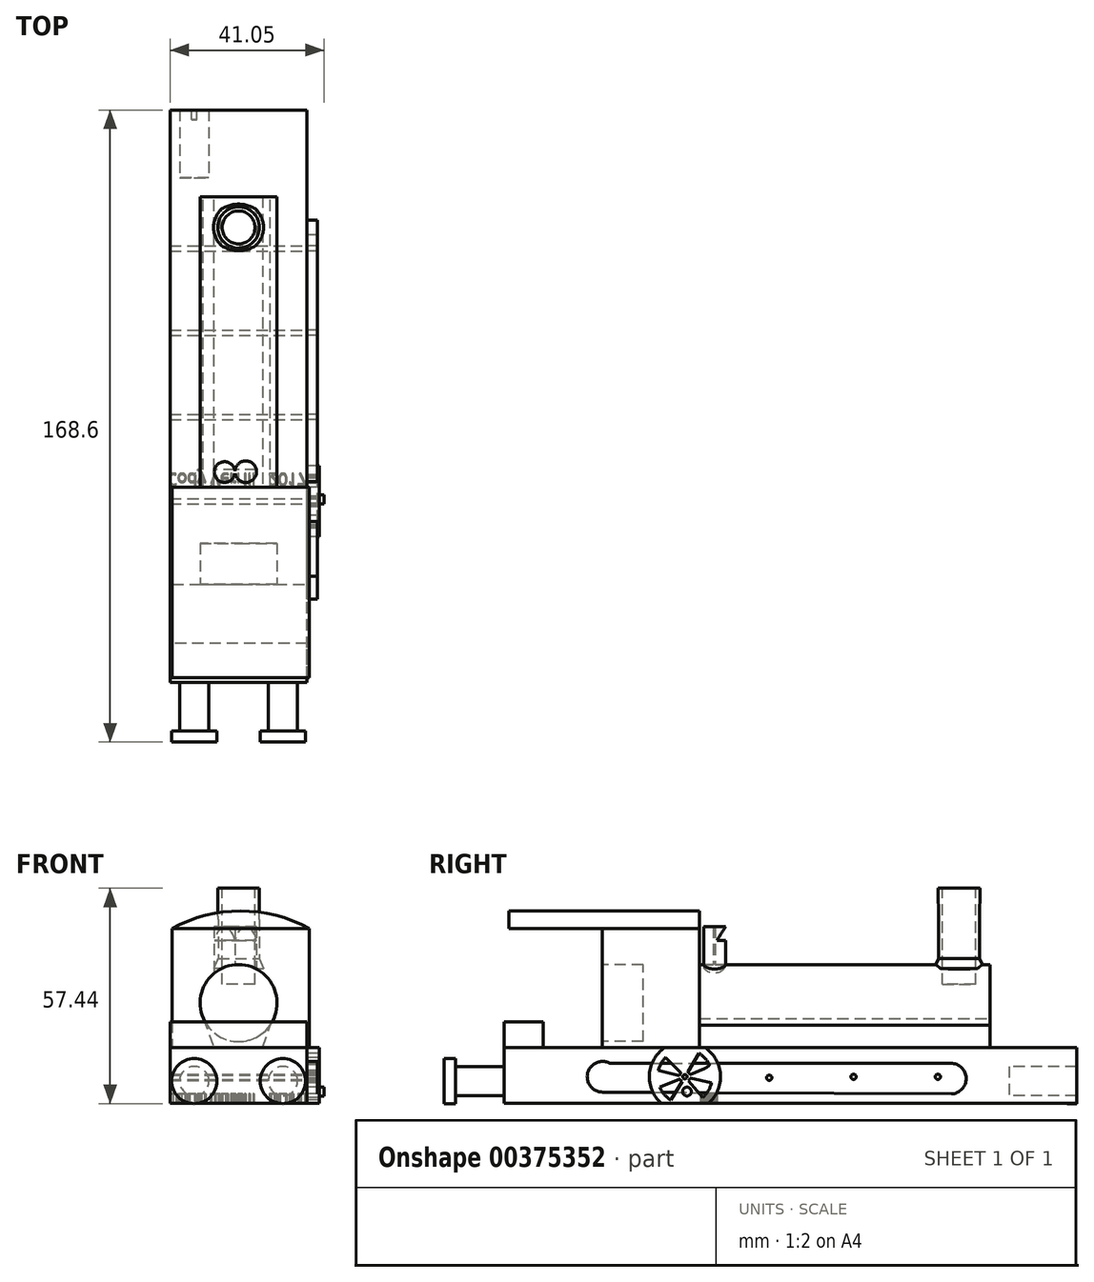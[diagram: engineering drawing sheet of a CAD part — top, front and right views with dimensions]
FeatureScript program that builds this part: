
annotation { "Feature Type Name" : "Feature", "Feature Type Description" : "" }
export const myFeature = defineFeature(function(context is Context, id is Id, definition is map)
    precondition{}
    {
        {
            var Q0;
            Q0=qCreatedBy(makeId("Front.planeOp"),FACE);
            var sketch = newSketch(context, id + "F0", { "sketchPlane" : qUnion([Q0])});
            skCircle(sketch, "E0", {"center": v(0, 91.63) * mm, "radius": 10.27 * mm});
            skSolve(sketch);
        }
        {
            var Q0;
            Q0=makeQuery(id+"F0.imprint","IMPRINT",FACE,{"disambiguationData":[TD([[makeQuery(id+"F0.imprint","IMPRINT",EDGE,{"derivedFrom":sQuery(id+"F0.wireOp",EDGE,"E0")}),1.0]])]});
            extrude(context, id + "F1", {"entities" : qUnion([Q0]), "depth" : 77.47 * mm});
        }
        {
            var Q0;
            Q0=makeQuery(id+"F1.opExtrude","CAP_FACE",FACE,{"disambiguationData":[OSD([sQuery(id+"F0.wireOp",EDGE,"E0")])],"isStart":false});
            var sketch = newSketch(context, id + "F2", { "sketchPlane" : qUnion([Q0])});
            skLineSegment(sketch, "E1.bottom", {"start": v(-17.68, 111.5) * mm, "end": v(18.8, 111.5) * mm});
            skLineSegment(sketch, "E1.top", {"start": v(-17.68, 79.8) * mm, "end": v(18.8, 79.8) * mm});
            skLineSegment(sketch, "E1.left", {"start": v(-17.68, 111.5) * mm, "end": v(-17.68, 79.8) * mm});
            skLineSegment(sketch, "E1.right", {"start": v(18.8, 111.5) * mm, "end": v(18.8, 79.8) * mm});
            skArc(sketch, "E2", {"start": v(18.8, 111.5) * mm, "mid": v(0.56, 116.2) * mm, "end": v(-17.68, 111.5) * mm});
            skSolve(sketch);
        }
        {
            var Q0;
            Q0=makeQuery(id+"F2.imprint","IMPRINT",FACE,{"disambiguationData":[TD([[makeQuery(id+"F2.imprint","IMPRINT",EDGE,{"derivedFrom":sQuery(id+"F2.wireOp",EDGE,"E1.bottom")}),1.0]])]});
            var Q1;
            Q1=makeQuery(id+"F2.imprint","IMPRINT",FACE,{"disambiguationData":[TD([[makeQuery(id+"F2.imprint","IMPRINT",EDGE,{"derivedFrom":sQuery(id+"F2.wireOp",EDGE,"E1.bottom")}),-1.0]])]});
            var Q2;
            Q2=makeQuery(id+"F2.imprint","IMPRINT",FACE,{"disambiguationData":[TD([[makeQuery(id+"F2.imprint","IMPRINT",EDGE,{"derivedFrom":makeQuery(id+"F1.opExtrude","CAP_EDGE",EDGE,{"disambiguationData":[OSD([sQuery(id+"F0.wireOp",EDGE,"E0")])],"isStart":false})}),1.0]])]});
            extrude(context, id + "F3", {"entities" : qUnion([Q0, Q1, Q2]), "depth" : 25.9 * mm});
        }
        {
            var Q0;
            Q0=makeQuery(id+"F3.opExtrude","CAP_FACE",FACE,{"disambiguationData":[OSD([sQuery(id+"F0.wireOp",EDGE,"E0"),sQuery(id+"F2.wireOp",EDGE,"E1.top"),sQuery(id+"F2.wireOp",EDGE,"E1.left"),sQuery(id+"F2.wireOp",EDGE,"E1.right"),sQuery(id+"F2.wireOp",EDGE,"E2")])],"isStart":false});
            var sketch = newSketch(context, id + "F4", { "sketchPlane" : qUnion([Q0])});
            skLineSegment(sketch, "E3", {"start": v(-17.68, 111.5) * mm, "end": v(18.8, 111.5) * mm});
            skSolve(sketch);
        }
        {
            var Q0;
            Q0=makeQuery(id+"F4.imprint","IMPRINT",FACE,{"disambiguationData":[TD([[makeQuery(id+"F4.imprint","IMPRINT",EDGE,{"derivedFrom":sQuery(id+"F4.wireOp",EDGE,"E3")}),1.0]])]});
            extrude(context, id + "F5", {"entities" : qUnion([Q0]), "operationType" : NewBodyOperationType.ADD, "depth" : 24.9 * mm});
        }
        {
            var Q0;
            Q0=qCreatedBy(makeId("Front.planeOp"),FACE);
            var sketch = newSketch(context, id + "F6", { "sketchPlane" : qUnion([Q0])});
            skLineSegment(sketch, "E4.top", {"start": v(14.24, 65.38) * mm, "end": v(-13.5, 65.38) * mm});
            skLineSegment(sketch, "E4.left", {"start": v(14.24, 78.57) * mm, "end": v(14.24, 65.38) * mm});
            skLineSegment(sketch, "E4.right", {"start": v(-13.5, 78.57) * mm, "end": v(-13.5, 65.38) * mm});
            skLineSegment(sketch, "E5", {"start": v(14.24, 78.57) * mm, "end": v(-13.5, 78.57) * mm});
            skLineSegment(sketch, "E6", {"start": v(-9.81, 88.6) * mm, "end": v(-6.1, 78.57) * mm});
            skCircle(sketch, "E7.0", {"center": v(0, 91.63) * mm, "radius": 10.27 * mm});
            skLineSegment(sketch, "E8", {"start": v(6.01, 78.57) * mm, "end": v(8.4, 85.72) * mm});
            skSolve(sketch);
        }
        {
            var Q0;
            Q0=makeQuery(id+"F6.imprint","IMPRINT",FACE,{"disambiguationData":[TD([[makeQuery(id+"F6.imprint","IMPRINT",EDGE,{"derivedFrom":sQuery(id+"F6.wireOp",EDGE,"E4.top")}),-1.0]])]});
            var Q1;
            {var subQ3=sQuery(id+"F6.wireOp",EDGE,"E8");Q1=makeQuery(id+"F6.imprint","IMPRINT",FACE,{"disambiguationData":[TD([[makeQuery(id+"F6.imprint","IMPRINT",EDGE,{"derivedFrom":subQ3}),1.0]])]});}
            extrude(context, id + "F7", {"entities" : qUnion([Q0, Q1]), "operationType" : NewBodyOperationType.ADD, "depth" : 78.74 * mm});
        }
        {
            var Q0;
            Q0=qCreatedBy(makeId("Front.planeOp"),FACE);
            var sketch = newSketch(context, id + "F8", { "sketchPlane" : qUnion([Q0])});
            skLineSegment(sketch, "E9.bottom", {"start": v(18.25, 79.8) * mm, "end": v(-18.25, 79.8) * mm});
            skLineSegment(sketch, "E9.left", {"start": v(18.25, 79.8) * mm, "end": v(18.25, 64.86) * mm});
            skLineSegment(sketch, "E9.right", {"start": v(-18.25, 79.8) * mm, "end": v(-18.25, 64.86) * mm});
            skLineSegment(sketch, "E10", {"start": v(-18.25, 64.86) * mm, "end": v(18.25, 64.86) * mm});
            skSolve(sketch);
        }
        {
            var Q0;
            Q0 = qSketchRegion(id + "F8", true);
            extrude(context, id + "F9", {"entities" : qUnion([Q0]), "operationType" : NewBodyOperationType.ADD, "depth" : 129.54 * mm, "hasSecondDirection" : true, "secondDirectionOppositeDirection" : true, "secondDirectionDepth" : 5.08 * mm});
        }
        {
            var Q0;
            Q0=qCreatedBy(makeId("Top.planeOp"),FACE);
            cPlane(context, id + "F10", {"entities" : qUnion([Q0]), "cplaneType" : CPlaneType.OFFSET, "offset" : 95.25 * mm, "width" : 152.4 * mm, "height" : 152.4 * mm});
        }
        {
            var Q0;
            Q0=qCreatedBy(id+"F10.planeOp",FACE);
            var sketch = newSketch(context, id + "F11", { "sketchPlane" : qUnion([Q0])});
            skCircle(sketch, "E11", {"center": v(1.92, -73.37) * mm, "radius": 2.88 * mm});
            skCircle(sketch, "E12", {"center": v(-3.73, -73.47) * mm, "radius": 2.77 * mm});
            skLineSegment(sketch, "E13.bottom", {"start": v(-0.4, -73.79) * mm, "end": v(-2.1, -73.79) * mm});
            skLineSegment(sketch, "E13.top", {"start": v(-0.4, -73.24) * mm, "end": v(-2.1, -73.24) * mm});
            skLineSegment(sketch, "E13.left", {"start": v(-0.4, -73.79) * mm, "end": v(-0.4, -73.24) * mm});
            skLineSegment(sketch, "E13.right", {"start": v(-2.1, -73.79) * mm, "end": v(-2.1, -73.24) * mm});
            skPoint(sketch, "E13.middle", {"position": v(-1.25, -73.52) * mm});
            skSolve(sketch);
        }
        {
            var Q0;
            Q0 = qSketchRegion(id + "F11", true);
            extrude(context, id + "F12", {"entities" : qUnion([Q0]), "operationType" : NewBodyOperationType.ADD, "depth" : 16.76 * mm});
        }
        {
            var Q0;
            Q0=qCreatedBy(makeId("Right.planeOp"),FACE);
            var sketch = newSketch(context, id + "F13", { "sketchPlane" : qUnion([Q0])});
            skLineSegment(sketch, "E14", {"start": v(-70.17, 108.34) * mm, "end": v(-72.79, 108.34) * mm});
            skLineSegment(sketch, "E15", {"start": v(-72.79, 108.34) * mm, "end": v(-70.1, 112.6) * mm});
            skLineSegment(sketch, "E16", {"start": v(-70.1, 112.6) * mm, "end": v(-70.17, 108.34) * mm});
            skSolve(sketch);
        }
        {
            var Q0;
            Q0=makeQuery(id+"F13.imprint","IMPRINT",FACE,{"disambiguationData":[TD([[makeQuery(id+"F13.imprint","IMPRINT",EDGE,{"derivedFrom":sQuery(id+"F13.wireOp",EDGE,"E14")}),-1.0]])]});
            extrude(context, id + "F14", {"entities" : qUnion([Q0]), "operationType" : NewBodyOperationType.REMOVE, "endBound" : BoundingType.THROUGH_ALL, "depth" : 25.4 * mm, "hasSecondDirection" : true, "secondDirectionBound" : SecondDirectionBoundingType.THROUGH_ALL, "secondDirectionOppositeDirection" : true, "secondDirectionDepth" : 25.4 * mm});
        }
        {
            var Q0;
            Q0=makeQuery(id+"F13.imprint","IMPRINT",FACE,{"disambiguationData":[TD([[makeQuery(id+"F13.imprint","IMPRINT",EDGE,{"derivedFrom":sQuery(id+"F13.wireOp",EDGE,"E14")}),-1.0]])]});
            extrude(context, id + "F15", {"entities" : qUnion([Q0]), "operationType" : NewBodyOperationType.REMOVE, "depth" : 25.4 * mm});
        }
        {
            var Q0;
            Q0=qCreatedBy(makeId("Right.planeOp"),FACE);
            var sketch = newSketch(context, id + "F16", { "sketchPlane" : qUnion([Q0])});
            skLineSegment(sketch, "E17", {"start": v(-2.75, 113.9) * mm, "end": v(-2.75, 103.55) * mm});
            skLineSegment(sketch, "E18", {"start": v(-2.75, 103.55) * mm, "end": v(-1.55, 100.87) * mm});
            skLineSegment(sketch, "E19", {"start": v(-8.2, 100.22) * mm, "end": v(-1.55, 100.87) * mm});
            skLineSegment(sketch, "E20", {"start": v(-8.2, 100.22) * mm, "end": v(-8.2, 122.25) * mm});
            skLineSegment(sketch, "E21", {"start": v(-8.2, 122.25) * mm, "end": v(-2.67, 122.25) * mm});
            skLineSegment(sketch, "E22", {"start": v(-2.75, 113.9) * mm, "end": v(-2.67, 122.25) * mm});
            skSolve(sketch);
        }
        {
            var Q0;
            Q0=makeQuery(id+"F16.imprint","IMPRINT",FACE,{"disambiguationData":[TD([[makeQuery(id+"F16.imprint","IMPRINT",EDGE,{"derivedFrom":sQuery(id+"F16.wireOp",EDGE,"E17")}),-1.0]])]});
            var Q1;
            Q1=sQuery(id+"F16.wireOp",EDGE,"E20");
            revolve(context, id + "F17", {"operationType" : NewBodyOperationType.ADD, "entities" : qUnion([Q0]), "axis" : qUnion([Q1]), "revolveType" : RevolveType.FULL});
        }
        {
            var Q0;
            Q0=makeQuery(id+"F9.opExtrude","SWEPT_FACE",FACE,{"disambiguationData":[OSD([sQuery(id+"F8.wireOp",EDGE,"E9.left")])]});
            var sketch = newSketch(context, id + "F18", { "sketchPlane" : qUnion([Q0])});
            skPoint(sketch, "E23.center", {"position": v(0, 0) * mm});
            skLineSegment(sketch, "E24", {"start": v(-79.94, 72.54) * mm, "end": v(-76, 74.2) * mm});
            skArc(sketch, "E25", {"start": v(-88, 69.15) * mm, "mid": v(-86.8, 67.22) * mm, "end": v(-85.06, 65.75) * mm});
            skLineSegment(sketch, "E26.1.0", {"start": v(-80.54, 73.23) * mm, "end": v(-77.53, 78.2) * mm});
            skLineSegment(sketch, "E26.4.0", {"start": v(-82.73, 72.3) * mm, "end": v(-88.38, 73.63) * mm});
            skLineSegment(sketch, "E26.5.0", {"start": v(-82.65, 71.4) * mm, "end": v(-88, 69.15) * mm});
            skLineSegment(sketch, "E26.6.0", {"start": v(-82.06, 70.71) * mm, "end": v(-85.06, 65.75) * mm});
            skLineSegment(sketch, "E26.8.0", {"start": v(-80.34, 70.86) * mm, "end": v(-76.54, 66.47) * mm});
            skLineSegment(sketch, "E26.9.0", {"start": v(-79.87, 71.63) * mm, "end": v(-74.22, 70.31) * mm});
            skPoint(sketch, "E27.center.orphan", {"position": v(-44.54, 71.07) * mm});
            skCircle(sketch, "E28.MirrorC", {"center": v(-61.62, 71.97) * mm, "radius": 7.27 * mm});
            skLineSegment(sketch, "E29.MirrorCS", {"start": v(-61.62, 71.97) * mm, "end": v(-55.37, 73.17) * mm});
            skLineSegment(sketch, "E30.MirrorCS", {"start": v(-61.62, 71.97) * mm, "end": v(-57.27, 76.61) * mm});
            skLineSegment(sketch, "E31.MirrorCS", {"start": v(-61.62, 71.97) * mm, "end": v(-60.83, 78.28) * mm});
            skLineSegment(sketch, "E32.MirrorCS", {"start": v(-61.62, 71.97) * mm, "end": v(-64.7, 77.54) * mm});
            skLineSegment(sketch, "E33.MirrorCS", {"start": v(-61.62, 71.97) * mm, "end": v(-67.38, 74.67) * mm});
            skLineSegment(sketch, "E34.MirrorCS", {"start": v(-61.62, 71.97) * mm, "end": v(-67.87, 70.77) * mm});
            skLineSegment(sketch, "E35.MirrorCS", {"start": v(-61.62, 71.97) * mm, "end": v(-65.97, 67.33) * mm});
            skLineSegment(sketch, "E36.MirrorCS", {"start": v(-61.62, 71.97) * mm, "end": v(-62.41, 65.66) * mm});
            skLineSegment(sketch, "E37.MirrorCS", {"start": v(-61.62, 71.97) * mm, "end": v(-58.55, 66.4) * mm});
            skLineSegment(sketch, "E38.MirrorCS", {"start": v(-61.62, 71.97) * mm, "end": v(-55.86, 69.27) * mm});
            skCircle(sketch, "E39.MirrorC", {"center": v(-61.73, 71.74) * mm, "radius": 6.37 * mm});
            skLineSegment(sketch, "E40.MirrorCS", {"start": v(-43.2, 71.97) * mm, "end": v(-47.55, 76.61) * mm});
            skLineSegment(sketch, "E41.MirrorCS", {"start": v(-43.2, 71.97) * mm, "end": v(-43.99, 78.28) * mm});
            skLineSegment(sketch, "E42.MirrorCS", {"start": v(-43.2, 71.97) * mm, "end": v(-40.13, 77.54) * mm});
            skLineSegment(sketch, "E43.MirrorCS", {"start": v(-43.2, 71.97) * mm, "end": v(-37.44, 74.67) * mm});
            skLineSegment(sketch, "E44.MirrorCS", {"start": v(-43.2, 71.97) * mm, "end": v(-36.95, 70.77) * mm});
            skLineSegment(sketch, "E45.MirrorCS", {"start": v(-43.2, 71.97) * mm, "end": v(-38.85, 67.33) * mm});
            skLineSegment(sketch, "E46.MirrorCS", {"start": v(-43.2, 71.97) * mm, "end": v(-42.4, 65.66) * mm});
            skLineSegment(sketch, "E47.MirrorCS", {"start": v(-43.2, 71.97) * mm, "end": v(-48.96, 69.27) * mm});
            skLineSegment(sketch, "E48.MirrorCS", {"start": v(-43.2, 71.97) * mm, "end": v(-49.45, 73.17) * mm});
            skCircle(sketch, "E49.MirrorC", {"center": v(-43.1, 71.74) * mm, "radius": 6.37 * mm});
            skCircle(sketch, "E50.MirrorC", {"center": v(-43.2, 71.97) * mm, "radius": 7.27 * mm});
            skLineSegment(sketch, "E51", {"start": v(-43.1, 71.74) * mm, "end": v(-47.38, 67.03) * mm});
            skArc(sketch, "E52", {"start": v(-82.65, 71.4) * mm, "mid": v(-82.41, 71) * mm, "end": v(-82.06, 70.71) * mm});
            skArc(sketch, "E53.trimOffspring", {"start": v(-82.35, 73) * mm, "mid": v(-82.59, 72.68) * mm, "end": v(-82.73, 72.3) * mm});
            skArc(sketch, "E54.trimOffspring", {"start": v(-79.94, 72.54) * mm, "mid": v(-80.19, 72.93) * mm, "end": v(-80.54, 73.23) * mm});
            skArc(sketch, "E55.trimOffspring", {"start": v(-80.34, 70.86) * mm, "mid": v(-80.04, 71.2) * mm, "end": v(-79.87, 71.63) * mm});
            skCircle(sketch, "E56", {"center": v(-81.3, 71.97) * mm, "radius": 0.57 * mm});
            skArc(sketch, "E57.filletArc", {"start": v(-76, 74.2) * mm, "mid": v(-75.32, 74.6) * mm, "end": v(-74.75, 75.13) * mm});
            skLineSegment(sketch, "E58", {"start": v(-86.49, 77.07) * mm, "end": v(-82.35, 73) * mm});
            skArc(sketch, "E59.trimOffspring", {"start": v(-86.49, 77.07) * mm, "mid": v(-87.67, 75.48) * mm, "end": v(-88.38, 73.63) * mm});
            skArc(sketch, "E60.trimOffspring", {"start": v(-76.54, 66.47) * mm, "mid": v(-75.08, 68.2) * mm, "end": v(-74.22, 70.31) * mm});
            skArc(sketch, "E61.trimOffspring", {"start": v(-74.75, 75.13) * mm, "mid": v(-75.92, 76.86) * mm, "end": v(-77.53, 78.2) * mm});
            skCircle(sketch, "E62", {"center": v(-81.3, 71.97) * mm, "radius": 9.47 * mm});
            skCircle(sketch, "E63", {"center": v(-81.3, 71.97) * mm, "radius": 7.27 * mm, "construction": true});
            skSolve(sketch);
        }
        {
            var Q0;
            Q0=makeQuery(id+"F18.imprint","IMPRINT",FACE,{"disambiguationData":[TD([[makeQuery(id+"F18.imprint","IMPRINT",EDGE,{"derivedFrom":sQuery(id+"F18.wireOp",EDGE,"E24")}),-1.0]])]});
            var Q1;
            {var subQ0=sQuery(id+"F18.wireOp",EDGE,"E62");var subQ1=makeQuery(id+"F9.opExtrude","SWEPT_EDGE",EDGE,{"disambiguationData":[OSD([sQuery(id+"F8.wireOp",EDGE,"E9.left"),sQuery(id+"F8.wireOp",EDGE,"E10")])]});var subQ2=makeQuery(id+"F18.imprint","INTERSECT",VERTEX,{"disambiguationData":[OD(0.0)],"derivedFrom":[subQ1,subQ0]});Q1=makeQuery(id+"F18.imprint","IMPRINT",FACE,{"disambiguationData":[TD([[makeQuery(id+"F18.imprint","IMPRINT",EDGE,{"disambiguationData":[TD([[subQ2,-1.0]])],"derivedFrom":subQ0}),1.0]])]});}
            var Q2;
            {var subQ0=sQuery(id+"F18.wireOp",EDGE,"E62");var subQ1=makeQuery(id+"F9.opExtrude","SWEPT_EDGE",EDGE,{"disambiguationData":[OSD([sQuery(id+"F8.wireOp",EDGE,"E9.bottom"),sQuery(id+"F8.wireOp",EDGE,"E9.left")])]});var subQ2=makeQuery(id+"F18.imprint","INTERSECT",VERTEX,{"disambiguationData":[OD(0.0)],"derivedFrom":[subQ1,subQ0]});Q2=makeQuery(id+"F18.imprint","IMPRINT",FACE,{"disambiguationData":[TD([[makeQuery(id+"F18.imprint","IMPRINT",EDGE,{"disambiguationData":[TD([[subQ2,1.0]])],"derivedFrom":subQ0}),1.0]])]});}
            extrude(context, id + "F19", {"entities" : qUnion([Q0, Q1, Q2]), "depth" : 3.3 * mm});
        }
        {
            var Q0;
            {var subQ0=sQuery(id+"F8.wireOp",EDGE,"E9.left");var subQ11=makeQuery(id+"F9.opExtrude","CAP_EDGE",EDGE,{"disambiguationData":[OSD([subQ0])],"isStart":true});Q0=makeQuery(id+"F18.imprint","IMPRINT",FACE,{"disambiguationData":[TD([[makeQuery(id+"F18.imprint","IMPRINT",EDGE,{"derivedFrom":subQ11}),-1.0]])]});}
            var sketch = newSketch(context, id + "F20", { "sketchPlane" : qUnion([Q0])});
            skCircle(sketch, "E64", {"center": v(-81.3, 71.97) * mm, "radius": 0.7 * mm});
            skCircle(sketch, "E65.MirrorC", {"center": v(-36.34, 71.96) * mm, "radius": 0.7 * mm});
            skArc(sketch, "E66", {"start": v(-101.27, 75.56) * mm, "mid": v(-107.2, 72.99) * mm, "end": v(-103.26, 67.86) * mm});
            skPoint(sketch, "E67.MirrorC.center.orphan", {"position": v(-58.82, 71.71) * mm});
            skCircle(sketch, "E68", {"center": v(-58.82, 71.71) * mm, "radius": 0.7 * mm});
            skCircle(sketch, "E69", {"center": v(-13.86, 71.96) * mm, "radius": 0.7 * mm});
            skLineSegment(sketch, "E70", {"start": v(-101.27, 75.56) * mm, "end": v(-10.43, 75.56) * mm});
            skLineSegment(sketch, "E71", {"start": v(-103.26, 67.86) * mm, "end": v(-10.25, 67.37) * mm});
            skArc(sketch, "E72", {"start": v(-10.25, 67.37) * mm, "mid": v(-6.33, 71.55) * mm, "end": v(-10.43, 75.56) * mm});
            skSolve(sketch);
        }
        {
            var Q0;
            Q0=makeQuery(id+"F20.imprint","IMPRINT",FACE,{"disambiguationData":[TD([[makeQuery(id+"F20.imprint","IMPRINT",EDGE,{"derivedFrom":sQuery(id+"F20.wireOp",EDGE,"E68")}),1.0]])]});
            var Q1;
            Q1=makeQuery(id+"F20.imprint","IMPRINT",FACE,{"disambiguationData":[TD([[makeQuery(id+"F20.imprint","IMPRINT",EDGE,{"derivedFrom":sQuery(id+"F20.wireOp",EDGE,"E64")}),1.0]])]});
            var Q2;
            {var subQ0=sQuery(id+"F20.wireOp",EDGE,"E65.MirrorC");var subQ1=sQuery(id+"F18.wireOp",EDGE,"E50.MirrorC");var subQ2=makeQuery(id+"F9.opExtrude","SWEPT_EDGE",EDGE,{"disambiguationData":[OSD([sQuery(id+"F8.wireOp",EDGE,"E9.left"),sQuery(id+"F8.wireOp",EDGE,"E10")])]});var subQ3=makeQuery(id+"F18.imprint","IMPRINT",EDGE,{"disambiguationData":[TD([[makeQuery(id+"F18.imprint","INTERSECT",VERTEX,{"disambiguationData":[OD(0.0)],"derivedFrom":[subQ2,subQ1]}),-1.0]])],"derivedFrom":subQ1});var subQ4=makeQuery(id+"F20.imprint","INTERSECT",VERTEX,{"disambiguationData":[OD(0.0)],"derivedFrom":[subQ3,subQ0]});Q2=makeQuery(id+"F20.imprint","IMPRINT",FACE,{"disambiguationData":[TD([[makeQuery(id+"F20.imprint","IMPRINT",EDGE,{"disambiguationData":[TD([[subQ4,1.0]])],"derivedFrom":subQ0}),1.0]])]});}
            var Q3;
            {var subQ0=sQuery(id+"F20.wireOp",EDGE,"E65.MirrorC");var subQ1=sQuery(id+"F18.wireOp",EDGE,"E50.MirrorC");var subQ2=makeQuery(id+"F9.opExtrude","SWEPT_EDGE",EDGE,{"disambiguationData":[OSD([sQuery(id+"F8.wireOp",EDGE,"E9.left"),sQuery(id+"F8.wireOp",EDGE,"E10")])]});var subQ3=makeQuery(id+"F18.imprint","IMPRINT",EDGE,{"disambiguationData":[TD([[makeQuery(id+"F18.imprint","INTERSECT",VERTEX,{"disambiguationData":[OD(0.0)],"derivedFrom":[subQ2,subQ1]}),-1.0]])],"derivedFrom":subQ1});var subQ4=makeQuery(id+"F20.imprint","INTERSECT",VERTEX,{"disambiguationData":[OD(0.0)],"derivedFrom":[subQ3,subQ0]});Q3=makeQuery(id+"F20.imprint","IMPRINT",FACE,{"disambiguationData":[TD([[makeQuery(id+"F20.imprint","IMPRINT",EDGE,{"disambiguationData":[TD([[subQ4,-1.0]])],"derivedFrom":subQ0}),1.0]])]});}
            var Q4;
            Q4=makeQuery(id+"F20.imprint","IMPRINT",FACE,{"disambiguationData":[TD([[makeQuery(id+"F20.imprint","IMPRINT",EDGE,{"derivedFrom":sQuery(id+"F20.wireOp",EDGE,"E69")}),1.0]])]});
            extrude(context, id + "F21", {"entities" : qUnion([Q0, Q1, Q2, Q3, Q4]), "operationType" : NewBodyOperationType.REMOVE, "endBound" : BoundingType.THROUGH_ALL, "oppositeDirection" : true, "depth" : 25.4 * mm});
        }
        {
            var Q0;
            Q0 = qSketchRegion(id + "F20", true);
            extrude(context, id + "F22", {"entities" : qUnion([Q0]), "depth" : 2.8 * mm});
        }
        {
            var Q0;
            Q0=makeQuery(id+"F19.opExtrude","CAP_FACE",FACE,{"disambiguationData":[OSD([sQuery(id+"F8.wireOp",EDGE,"E9.left"),sQuery(id+"F8.wireOp",EDGE,"E10"),sQuery(id+"F18.wireOp",EDGE,"E24"),sQuery(id+"F18.wireOp",EDGE,"E25"),sQuery(id+"F18.wireOp",EDGE,"E26.1.0"),sQuery(id+"F18.wireOp",EDGE,"E26.4.0"),sQuery(id+"F18.wireOp",EDGE,"E26.5.0"),sQuery(id+"F18.wireOp",EDGE,"E26.6.0"),sQuery(id+"F18.wireOp",EDGE,"E26.8.0"),sQuery(id+"F18.wireOp",EDGE,"E26.9.0"),sQuery(id+"F18.wireOp",EDGE,"0c8bdb6e-3c98-4d02-b736-932f722b0c7a.trimOffspring"),sQuery(id+"F18.wireOp",EDGE,"1BuqDyHR-VqEz-mvgE-IeDF-BNDoeJWoOokS"),sQuery(id+"F18.wireOp",EDGE,"640e9c71-0b7e-4dc1-b20b-68745f9d8d1d.trimOffspring"),sQuery(id+"F18.wireOp",EDGE,"18493bf5-1e1e-4aa6-ba80-e87df5e9a334.trimOffspring"),sQuery(id+"F18.wireOp",EDGE,"E56"),sQuery(id+"F18.wireOp",EDGE,"fb07b3ba-5013-41e2-a678-10b8c0feb796.trimOffspring"),sQuery(id+"F18.wireOp",EDGE,"E57.filletArc"),sQuery(id+"F18.wireOp",EDGE,"E58"),sQuery(id+"F18.wireOp",EDGE,"E53.trimOffspring"),sQuery(id+"F18.wireOp",EDGE,"E55.trimOffspring"),sQuery(id+"F18.wireOp",EDGE,"E52"),sQuery(id+"F18.wireOp",EDGE,"E54.trimOffspring")])],"isStart":false});
            var sketch = newSketch(context, id + "F23", { "sketchPlane" : qUnion([Q0])});
            skCircle(sketch, "E73", {"center": v(-80.75, 68.01) * mm, "radius": 1.17 * mm});
            skSolve(sketch);
        }
        {
            var Q0;
            Q0=makeQuery(id+"F23.imprint","IMPRINT",FACE,{"disambiguationData":[TD([[makeQuery(id+"F23.imprint","IMPRINT",EDGE,{"derivedFrom":sQuery(id+"F23.wireOp",EDGE,"E73")}),1.0]])]});
            extrude(context, id + "F24", {"entities" : qUnion([Q0]), "operationType" : NewBodyOperationType.ADD, "depth" : 1.24 * mm});
        }
        {
            var Q0;
            Q0=makeQuery(id+"F17.opRevolve","SWEPT_FACE",FACE,{"disambiguationData":[OSD([sQuery(id+"F16.wireOp",EDGE,"E21")])]});
            var sketch = newSketch(context, id + "F25", { "sketchPlane" : qUnion([Q0])});
            skCircle(sketch, "E74", {"center": v(0, -8.2) * mm, "radius": 4.38 * mm});
            skSolve(sketch);
        }
        {
            var Q0;
            Q0=makeQuery(id+"F25.imprint","IMPRINT",FACE,{"disambiguationData":[TD([[makeQuery(id+"F25.imprint","IMPRINT",EDGE,{"derivedFrom":sQuery(id+"F25.wireOp",EDGE,"E74")}),1.0]])]});
            extrude(context, id + "F26", {"entities" : qUnion([Q0]), "operationType" : NewBodyOperationType.REMOVE, "oppositeDirection" : true, "depth" : 25.65 * mm});
        }
        {
            var Q0;
            Q0=makeQuery(id+"F9.opExtrude","CAP_FACE",FACE,{"disambiguationData":[OSD([sQuery(id+"F8.wireOp",EDGE,"E9.bottom"),sQuery(id+"F8.wireOp",EDGE,"E9.left"),sQuery(id+"F8.wireOp",EDGE,"E9.right"),sQuery(id+"F8.wireOp",EDGE,"E10")])],"isStart":true});
            var sketch = newSketch(context, id + "F27", { "sketchPlane" : qUnion([Q0])});
            skCircle(sketch, "E75", {"center": v(-11.82, 70.82) * mm, "radius": 3.9 * mm});
            skLineSegment(sketch, "E76", {"start": v(0, 78.45) * mm, "end": v(0, 64.86) * mm});
            skCircle(sketch, "E77.MirrorC", {"center": v(11.82, 70.82) * mm, "radius": 3.9 * mm});
            skSolve(sketch);
        }
        {
            var Q0;
            Q0=makeQuery(id+"F27.imprint","IMPRINT",FACE,{"disambiguationData":[TD([[makeQuery(id+"F27.imprint","IMPRINT",EDGE,{"derivedFrom":sQuery(id+"F27.wireOp",EDGE,"E75")}),1.0]])]});
            var Q1;
            Q1=makeQuery(id+"F27.imprint","IMPRINT",FACE,{"disambiguationData":[TD([[makeQuery(id+"F27.imprint","IMPRINT",EDGE,{"derivedFrom":sQuery(id+"F27.wireOp",EDGE,"E77.MirrorC")}),-1.0]])]});
            extrude(context, id + "F28", {"entities" : qUnion([Q0, Q1]), "operationType" : NewBodyOperationType.ADD, "depth" : 18.03 * mm});
        }
        {
            var Q0;
            Q0=makeQuery(id+"F28.opExtrude","CAP_FACE",FACE,{"disambiguationData":[OSD([sQuery(id+"F27.wireOp",EDGE,"E77.MirrorC")])],"isStart":false});
            var sketch = newSketch(context, id + "F29", { "sketchPlane" : qUnion([Q0])});
            skCircle(sketch, "E78", {"center": v(11.82, 70.82) * mm, "radius": 6.02 * mm});
            skCircle(sketch, "E79.0", {"center": v(-11.82, 70.82) * mm, "radius": 3.9 * mm});
            skCircle(sketch, "E80", {"center": v(-11.82, 70.82) * mm, "radius": 6.02 * mm});
            skSolve(sketch);
        }
        {
            var Q0;
            Q0=makeQuery(id+"F29.imprint","IMPRINT",FACE,{"disambiguationData":[TD([[makeQuery(id+"F29.imprint","IMPRINT",EDGE,{"derivedFrom":sQuery(id+"F29.wireOp",EDGE,"E79.0")}),-1.0]])]});
            var Q1;
            Q1=makeQuery(id+"F29.imprint","IMPRINT",FACE,{"disambiguationData":[TD([[makeQuery(id+"F29.imprint","IMPRINT",EDGE,{"derivedFrom":sQuery(id+"F29.wireOp",EDGE,"E78")}),1.0]])]});
            extrude(context, id + "F30", {"entities" : qUnion([Q0, Q1]), "operationType" : NewBodyOperationType.ADD, "oppositeDirection" : true, "depth" : 2.54 * mm});
        }
        {
            var Q0;
            Q0=makeQuery(id+"F9.opExtrude","CAP_FACE",FACE,{"disambiguationData":[OSD([sQuery(id+"F8.wireOp",EDGE,"E9.bottom"),sQuery(id+"F8.wireOp",EDGE,"E9.left"),sQuery(id+"F8.wireOp",EDGE,"E9.right"),sQuery(id+"F8.wireOp",EDGE,"E10")])],"isStart":false});
            var sketch = newSketch(context, id + "F31", { "sketchPlane" : qUnion([Q0])});
            skPoint(sketch, "E81.endSnap0", {"position": v(0, 79.8) * mm});
            skCircle(sketch, "E82.0", {"center": v(-11.82, 70.82) * mm, "radius": 3.9 * mm});
            skCircle(sketch, "E83.0", {"center": v(11.82, 70.82) * mm, "radius": 3.9 * mm});
            skSolve(sketch);
        }
        {
            var Q0;
            Q0=makeQuery(id+"F31.imprint","IMPRINT",FACE,{"disambiguationData":[TD([[makeQuery(id+"F31.imprint","IMPRINT",EDGE,{"derivedFrom":sQuery(id+"F31.wireOp",EDGE,"E82.0")}),1.0]])]});
            var Q1;
            Q1=makeQuery(id+"F31.imprint","IMPRINT",FACE,{"disambiguationData":[TD([[makeQuery(id+"F31.imprint","IMPRINT",EDGE,{"derivedFrom":sQuery(id+"F31.wireOp",EDGE,"E83.0")}),1.0]])]});
            extrude(context, id + "F32", {"entities" : qUnion([Q0, Q1]), "operationType" : NewBodyOperationType.ADD, "depth" : 12.95 * mm});
        }
        {
            var Q0;
            Q0=makeQuery(id+"F32.opExtrude","CAP_FACE",FACE,{"disambiguationData":[OSD([sQuery(id+"F31.wireOp",EDGE,"E82.0")])],"isStart":false});
            var sketch = newSketch(context, id + "F33", { "sketchPlane" : qUnion([Q0])});
            skCircle(sketch, "E84.0.0", {"center": v(-11.82, 70.82) * mm, "radius": 6.02 * mm});
            skCircle(sketch, "E85.0", {"center": v(11.82, 70.82) * mm, "radius": 6.02 * mm});
            skSolve(sketch);
        }
        {
            var Q0;
            Q0=makeQuery(id+"F33.imprint","IMPRINT",FACE,{"disambiguationData":[TD([[makeQuery(id+"F33.imprint","IMPRINT",EDGE,{"derivedFrom":sQuery(id+"F33.wireOp",EDGE,"E85.0")}),1.0]])]});
            var Q1;
            Q1=makeQuery(id+"F33.imprint","IMPRINT",FACE,{"disambiguationData":[TD([[makeQuery(id+"F33.imprint","IMPRINT",EDGE,{"derivedFrom":sQuery(id+"F33.wireOp",EDGE,"E84.0.0")}),1.0]])]});
            var Q2;
            Q2=makeQuery(id+"F33.imprint","IMPRINT",FACE,{"disambiguationData":[TD([[makeQuery(id+"F33.imprint","IMPRINT",EDGE,{"derivedFrom":makeQuery(id+"F32.opExtrude","CAP_EDGE",EDGE,{"disambiguationData":[OSD([sQuery(id+"F31.wireOp",EDGE,"E82.0")])],"isStart":false})}),1.0]])]});
            extrude(context, id + "F34", {"entities" : qUnion([Q0, Q1, Q2]), "operationType" : NewBodyOperationType.ADD, "depth" : 3 * mm});
        }
        {
            var Q0;
            Q0=makeQuery(id+"F9.opExtrude","SWEPT_FACE",FACE,{"disambiguationData":[OSD([sQuery(id+"F8.wireOp",EDGE,"E9.bottom")])]});
            var sketch = newSketch(context, id + "F35", { "sketchPlane" : qUnion([Q0])});
            skLineSegment(sketch, "E86.bottom", {"start": v(18.08, -41.74) * mm, "end": v(-18.08, -41.74) * mm});
            skLineSegment(sketch, "E86.left", {"start": v(18.08, -41.74) * mm, "end": v(18.08, -52.62) * mm});
            skLineSegment(sketch, "E87", {"start": v(-18.08, -41.74) * mm, "end": v(-18.08, -49.9) * mm});
            skLineSegment(sketch, "E88", {"start": v(-18.08, -49.9) * mm, "end": v(18.08, -49.9) * mm});
            skLineSegment(sketch, "E89", {"start": v(18.08, -49.9) * mm, "end": v(18.08, -41.74) * mm});
            skLineSegment(sketch, "E90.bottom", {"start": v(18.25, -119.14) * mm, "end": v(-18.25, -119.14) * mm});
            skLineSegment(sketch, "E90.top", {"start": v(18.25, -129.53) * mm, "end": v(-18.25, -129.53) * mm});
            skLineSegment(sketch, "E90.left", {"start": v(18.25, -119.14) * mm, "end": v(18.25, -129.53) * mm});
            skLineSegment(sketch, "E90.right", {"start": v(-18.25, -119.14) * mm, "end": v(-18.25, -129.53) * mm});
            skPoint(sketch, "E90.middle", {"position": v(0, -124.34) * mm});
            skSolve(sketch);
        }
        {
            var Q0;
            {var subQ0=sQuery(id+"F35.wireOp",EDGE,"E90.bottom");var subQ1=sQuery(id+"F8.wireOp",EDGE,"E9.bottom");var subQ2=makeQuery(id+"F9.opExtrude","SWEPT_EDGE",EDGE,{"disambiguationData":[OSD([subQ1,sQuery(id+"F8.wireOp",EDGE,"E9.left")])]});var subQ3=makeQuery(id+"F35.imprint","INTERSECT",VERTEX,{"derivedFrom":[subQ2,subQ0]});Q0=makeQuery(id+"F35.imprint","IMPRINT",FACE,{"disambiguationData":[TD([[makeQuery(id+"F35.imprint","IMPRINT",EDGE,{"disambiguationData":[TD([[subQ3,-1.0]])],"derivedFrom":subQ0}),1.0]])]});}
            extrude(context, id + "F36", {"entities" : qUnion([Q0]), "depth" : 6.86 * mm});
        }
        {
            var Q0;
            Q0=makeQuery(id+"F4.imprint","IMPRINT",FACE,{"disambiguationData":[TD([[makeQuery(id+"F4.imprint","IMPRINT",EDGE,{"derivedFrom":sQuery(id+"F4.wireOp",EDGE,"E3")}),-1.0]])]});
            var sketch = newSketch(context, id + "F37", { "sketchPlane" : qUnion([Q0])});
            skCircle(sketch, "E91.0", {"center": v(0, 91.63) * mm, "radius": 10.27 * mm});
            skSolve(sketch);
        }
        {
            var Q0;
            Q0=makeQuery(id+"F37.imprint","IMPRINT",FACE,{"disambiguationData":[TD([[makeQuery(id+"F37.imprint","IMPRINT",EDGE,{"derivedFrom":sQuery(id+"F37.wireOp",EDGE,"E91.0")}),1.0]])]});
            extrude(context, id + "F38", {"entities" : qUnion([Q0]), "operationType" : NewBodyOperationType.REMOVE, "oppositeDirection" : true, "depth" : 10.92 * mm});
        }
        {
            var Q0;
            Q0=makeQuery(id+"F9.opExtrude","SWEPT_FACE",FACE,{"disambiguationData":[OSD([sQuery(id+"F8.wireOp",EDGE,"E10")])]});
            var sketch = newSketch(context, id + "F39", { "sketchPlane" : qUnion([Q0])});
            skText(sketch, "E92", { "text": "Cody Verrill   2017 ", "fontName": "OpenSans-Regular.ttf"});
            const initialGuessF39  = {"E92": [-0.0192, 0.07384, 1, 0, 0.0032]};
            skSetInitialGuess(sketch, initialGuessF39);
            skSolve(sketch);
        }
        {
            var Q0;
            Q0 = qSketchRegion(id + "F39", true);
            extrude(context, id + "F40", {"entities" : qUnion([Q0]), "operationType" : NewBodyOperationType.REMOVE, "oppositeDirection" : true, "depth" : 2.54 * mm});
        }
    });
